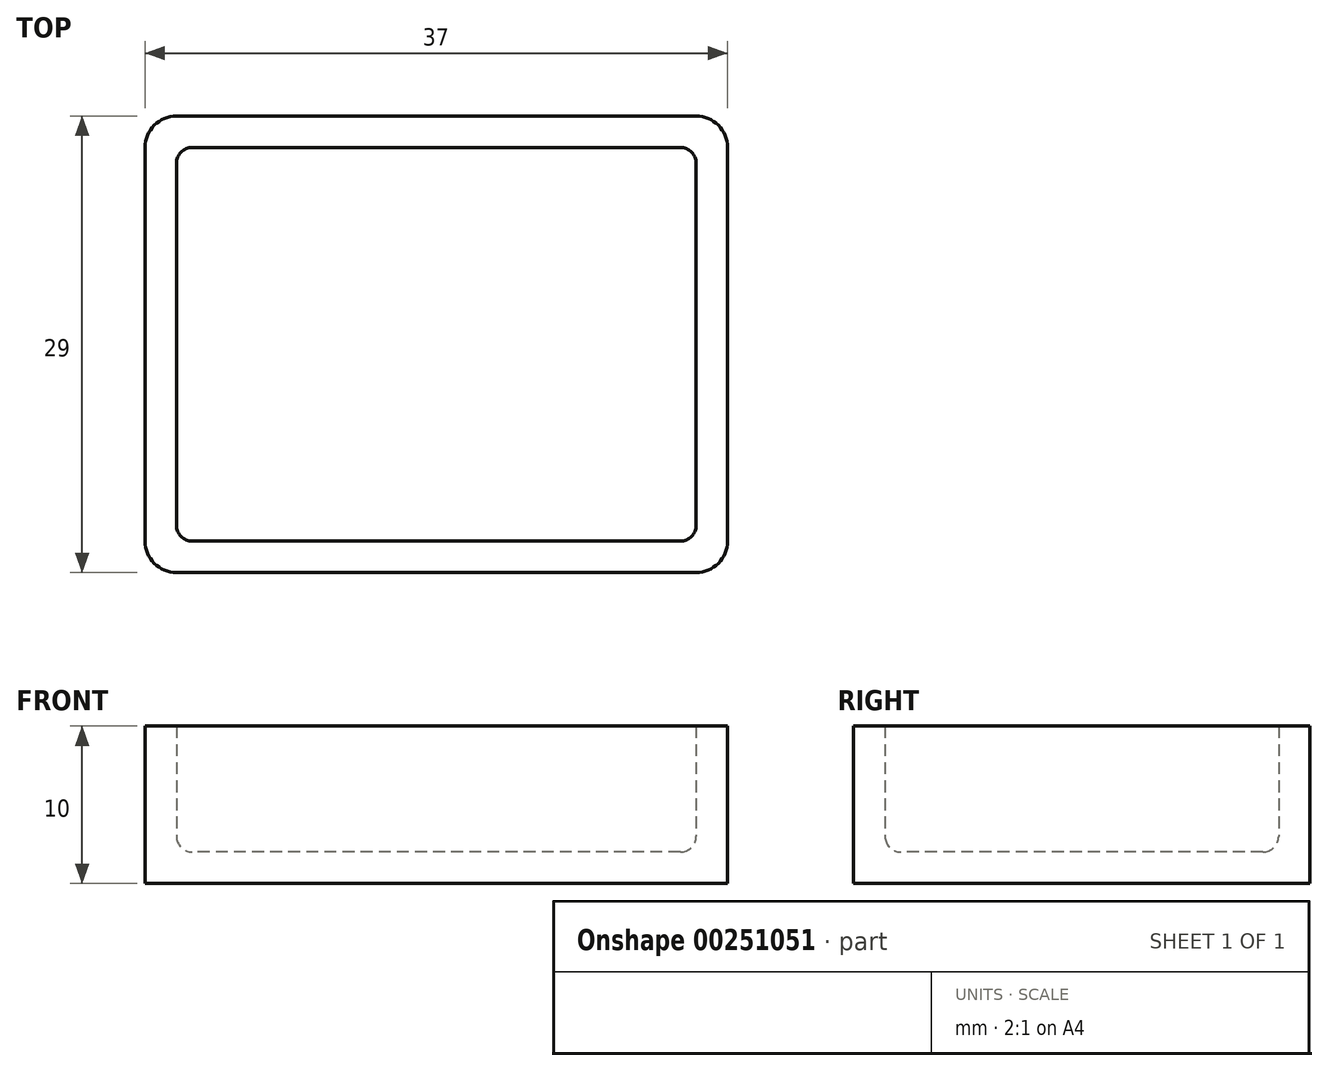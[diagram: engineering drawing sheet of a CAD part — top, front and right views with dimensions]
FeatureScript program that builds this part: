
annotation { "Feature Type Name" : "Feature", "Feature Type Description" : "" }
export const myFeature = defineFeature(function(context is Context, id is Id, definition is map)
    precondition{}
    {
        {
            var Q0;
            Q0=qCreatedBy(makeId("Top.planeOp"),FACE);
            var sketch = newSketch(context, id + "F0", { "sketchPlane" : qUnion([Q0])});
            skLineSegment(sketch, "E0", {"start": v(0, 14.5) * mm, "end": v(-16.5, 14.5) * mm});
            skLineSegment(sketch, "E1", {"start": v(-18.5, 12.5) * mm, "end": v(-18.5, 0) * mm});
            skPoint(sketch, "E2.visualSharp", {"position": v(-18.5, 14.5) * mm});
            skArc(sketch, "E2.filletArc", {"start": v(-16.5, 14.5) * mm, "mid": v(-17.91, 13.91) * mm, "end": v(-18.5, 12.5) * mm});
            skArc(sketch, "E3.MirrorCS", {"start": v(16.5, 14.5) * mm, "mid": v(17.91, 13.91) * mm, "end": v(18.5, 12.5) * mm});
            skPoint(sketch, "E4.MirrorP", {"position": v(18.5, 14.5) * mm});
            skLineSegment(sketch, "E5.MirrorCS", {"start": v(18.5, 12.5) * mm, "end": v(18.5, 0) * mm});
            skLineSegment(sketch, "E6.MirrorCS", {"start": v(0, 14.5) * mm, "end": v(16.5, 14.5) * mm});
            skArc(sketch, "E7.MirrorCS", {"start": v(-16.5, -14.5) * mm, "mid": v(-17.91, -13.91) * mm, "end": v(-18.5, -12.5) * mm});
            skArc(sketch, "E8.MirrorCS", {"start": v(16.5, -14.5) * mm, "mid": v(17.91, -13.91) * mm, "end": v(18.5, -12.5) * mm});
            skPoint(sketch, "E9.MirrorP", {"position": v(18.5, -14.5) * mm});
            skPoint(sketch, "E10.MirrorP", {"position": v(-18.5, -14.5) * mm});
            skLineSegment(sketch, "E11.MirrorCS", {"start": v(-18.5, -12.5) * mm, "end": v(-18.5, 0) * mm});
            skLineSegment(sketch, "E12.MirrorCS", {"start": v(18.5, -12.5) * mm, "end": v(18.5, 0) * mm});
            skLineSegment(sketch, "E13.MirrorCS", {"start": v(0, -14.5) * mm, "end": v(16.5, -14.5) * mm});
            skLineSegment(sketch, "E14.MirrorCS", {"start": v(0, -14.5) * mm, "end": v(-16.5, -14.5) * mm});
            skSolve(sketch);
        }
        {
            var Q0;
            Q0=makeQuery(id+"F0.imprint","IMPRINT",FACE,{"disambiguationData":[TD([[makeQuery(id+"F0.imprint","IMPRINT",EDGE,{"derivedFrom":sQuery(id+"F0.wireOp",EDGE,"E0")}),1.0]])]});
            extrude(context, id + "F1", {"entities" : qUnion([Q0]), "depth" : 10 * mm});
        }
        {
            var Q0;
            Q0=makeQuery(id+"F1.opExtrude","CAP_FACE",FACE,{"disambiguationData":[OSD([sQuery(id+"F0.wireOp",EDGE,"E0"),sQuery(id+"F0.wireOp",EDGE,"E1"),sQuery(id+"F0.wireOp",EDGE,"E2.filletArc"),sQuery(id+"F0.wireOp",EDGE,"E3.MirrorCS"),sQuery(id+"F0.wireOp",EDGE,"E5.MirrorCS"),sQuery(id+"F0.wireOp",EDGE,"E6.MirrorCS"),sQuery(id+"F0.wireOp",EDGE,"E7.MirrorCS"),sQuery(id+"F0.wireOp",EDGE,"E8.MirrorCS"),sQuery(id+"F0.wireOp",EDGE,"E11.MirrorCS"),sQuery(id+"F0.wireOp",EDGE,"E12.MirrorCS"),sQuery(id+"F0.wireOp",EDGE,"E13.MirrorCS"),sQuery(id+"F0.wireOp",EDGE,"E14.MirrorCS")])],"isStart":false});
            shell(context, id + "F2", {"entities" : qUnion([Q0]), "thickness" : 2 * mm});
        }
        {
            var Q0;
            Q0=makeQuery(id+"F2.opShell","OFFSET_EDGE",EDGE,{"disambiguationData":[OSD([sQuery(id+"F0.wireOp",EDGE,"E0"),sQuery(id+"F0.wireOp",EDGE,"E1"),sQuery(id+"F0.wireOp",EDGE,"E2.filletArc")])]});
            var Q1;
            {var subQ0=sQuery(id+"F0.wireOp",EDGE,"E6.MirrorCS");var subQ1=sQuery(id+"F0.wireOp",EDGE,"E0");Q1=makeQuery(id+"F2.opShell","OFFSET_EDGE",EDGE,{"disambiguationData":[OSD([subQ1,subQ0]),TDD([makeQuery(id+"F1.opExtrude","CAP_EDGE",EDGE,{"disambiguationData":[OSD([subQ1,subQ0])],"isStart":true})])]});}
            var Q2;
            {var subQ0=sQuery(id+"F0.wireOp",EDGE,"E11.MirrorCS");var subQ1=sQuery(id+"F0.wireOp",EDGE,"E1");Q2=makeQuery(id+"F2.opShell","OFFSET_EDGE",EDGE,{"disambiguationData":[OSD([subQ1,subQ0]),TDD([makeQuery(id+"F1.opExtrude","CAP_EDGE",EDGE,{"disambiguationData":[OSD([subQ1,subQ0])],"isStart":true})])]});}
            var Q3;
            Q3=makeQuery(id+"F2.opShell","OFFSET_EDGE",EDGE,{"disambiguationData":[OSD([sQuery(id+"F0.wireOp",EDGE,"E7.MirrorCS"),sQuery(id+"F0.wireOp",EDGE,"E11.MirrorCS"),sQuery(id+"F0.wireOp",EDGE,"E14.MirrorCS")])]});
            var Q4;
            Q4=makeQuery(id+"F2.opShell","OFFSET_FACE",FACE,{"disambiguationData":[OSD([sQuery(id+"F0.wireOp",EDGE,"E0"),sQuery(id+"F0.wireOp",EDGE,"E1"),sQuery(id+"F0.wireOp",EDGE,"E2.filletArc"),sQuery(id+"F0.wireOp",EDGE,"E3.MirrorCS"),sQuery(id+"F0.wireOp",EDGE,"E5.MirrorCS"),sQuery(id+"F0.wireOp",EDGE,"E6.MirrorCS"),sQuery(id+"F0.wireOp",EDGE,"E7.MirrorCS"),sQuery(id+"F0.wireOp",EDGE,"E8.MirrorCS"),sQuery(id+"F0.wireOp",EDGE,"E11.MirrorCS"),sQuery(id+"F0.wireOp",EDGE,"E12.MirrorCS"),sQuery(id+"F0.wireOp",EDGE,"E13.MirrorCS"),sQuery(id+"F0.wireOp",EDGE,"E14.MirrorCS")])]});
            var Q5;
            Q5=makeQuery(id+"F2.opShell","OFFSET_EDGE",EDGE,{"disambiguationData":[OSD([sQuery(id+"F0.wireOp",EDGE,"E8.MirrorCS"),sQuery(id+"F0.wireOp",EDGE,"E12.MirrorCS"),sQuery(id+"F0.wireOp",EDGE,"E13.MirrorCS")])]});
            var Q6;
            Q6=makeQuery(id+"F2.opShell","OFFSET_EDGE",EDGE,{"disambiguationData":[OSD([sQuery(id+"F0.wireOp",EDGE,"E3.MirrorCS"),sQuery(id+"F0.wireOp",EDGE,"E5.MirrorCS"),sQuery(id+"F0.wireOp",EDGE,"E6.MirrorCS")])]});
            fillet(context, id + "F3", {"entities" : qUnion([Q0, Q1, Q2, Q3, Q4, Q5, Q6]), "radius" : 1 * mm, "tangentPropagation" : true, "allowEdgeOverflow" : false});
        }
    });
